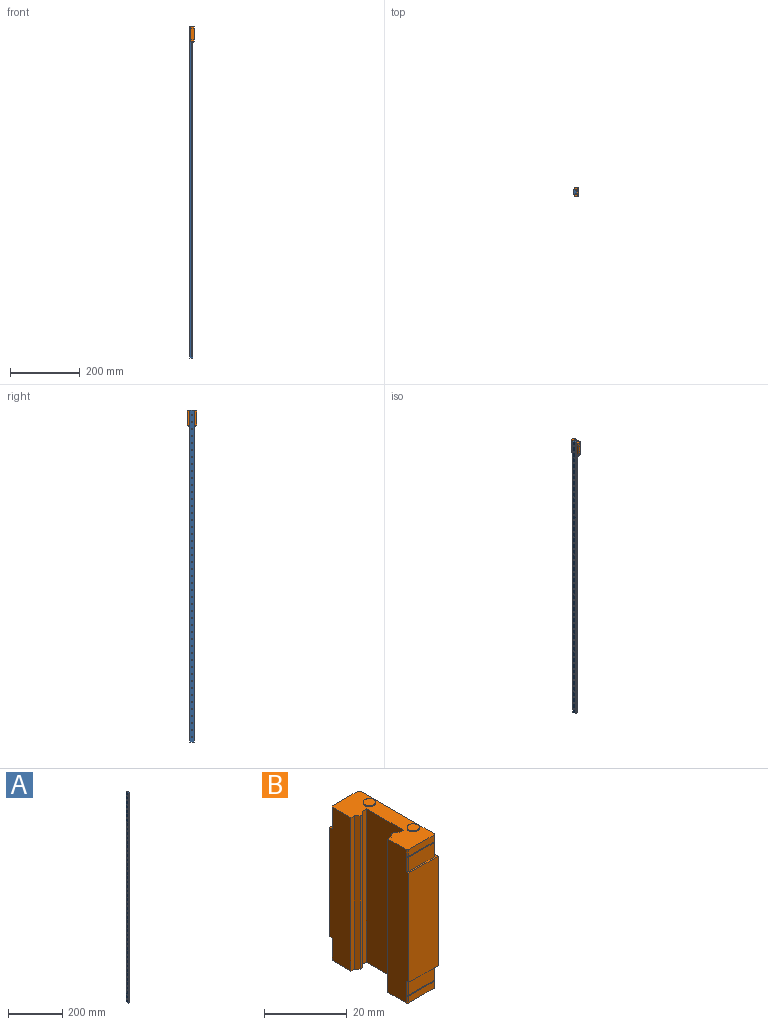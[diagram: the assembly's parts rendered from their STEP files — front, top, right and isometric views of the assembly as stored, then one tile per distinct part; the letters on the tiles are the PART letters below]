
ASSEMBLY  parts=2 mates=1
PART A: 155 faces, bbox 8x12x950 mm
  f0: plane 950x12mm, normal (1,0,0), area 10071.1mm2, adj f10,f11,f13,f15,f18,f21,f24,f27
  f1: cylinder r=1.75mm len=5.5mm, axis (-1,0,0), area 60.5mm2, adj f5,f14
  f2: plane 950x1mm, normal (0,1,0), area 950mm2, adj f3,f11,f12,f152
  f3: plane 950x1mm, normal (0.71,0.71,0), area 1343.5mm2, adj f2,f4,f11,f152
  f4: plane 950x4mm, normal (0,1,0), area 3800mm2, adj f3,f5,f11,f152
  f5: plane 950x12mm, normal (-1,0,0), area 10947.8mm2, adj f1,f4,f6,f11,f16,f19,f22,f25
  f6: plane 950x4mm, normal (0,-1,0), area 3800mm2, adj f5,f7,f11,f152
  f7: plane 950x1mm, normal (0.71,-0.71,0), area 1343.5mm2, adj f6,f8,f11,f152
  f8: plane 950x1mm, normal (0,-1,0), area 950mm2, adj f7,f9,f11,f152
  f9: plane 950x1mm, normal (-0.71,-0.71,0), area 1343.5mm2, adj f8,f10,f11,f152
  f10: plane 950x1mm, normal (0,-1,0), area 950mm2, adj f0,f9,f11,f152
  f11: plane 12x8mm, normal (0,0,-1), area 92mm2, adj f0,f2,f3,f4,f5,f6,f7,f8
  f12: plane 950x1mm, normal (-0.71,0.71,0), area 1343.5mm2, adj f2,f11,f13,f152
  f13: plane 950x1mm, normal (0,1,0), area 950mm2, adj f0,f11,f12,f152
  f14: plane 6x6mm, normal (1,0,0), area 18.7mm2, adj f1,f15
  f15: cylinder r=3mm len=6mm, axis (-1,0,0), area 47.1mm2, adj f0,f14
  f16: cylinder r=1.75mm len=5.5mm, axis (-1,0,0), area 60.5mm2, adj f5,f17
  f17: plane 6x6mm, normal (1,0,0), area 18.7mm2, adj f16,f18
  f18: cylinder r=3mm len=6mm, axis (-1,0,0), area 47.1mm2, adj f0,f17
  f19: cylinder r=1.75mm len=5.5mm, axis (-1,0,0), area 60.5mm2, adj f5,f20
  f20: plane 6x6mm, normal (1,0,0), area 18.7mm2, adj f19,f21
  f21: cylinder r=3mm len=6mm, axis (-1,0,0), area 47.1mm2, adj f0,f20
  f22: cylinder r=1.75mm len=5.5mm, axis (-1,0,0), area 60.5mm2, adj f5,f23
  f23: plane 6x6mm, normal (1,0,0), area 18.7mm2, adj f22,f24
  f24: cylinder r=3mm len=6mm, axis (-1,0,0), area 47.1mm2, adj f0,f23
  f25: cylinder r=1.75mm len=5.5mm, axis (-1,0,0), area 60.5mm2, adj f5,f26
  f26: plane 6x6mm, normal (1,0,0), area 18.7mm2, adj f25,f27
  f27: cylinder r=3mm len=6mm, axis (-1,0,0), area 47.1mm2, adj f0,f26
  f28: cylinder r=1.75mm len=5.5mm, axis (-1,0,0), area 60.5mm2, adj f5,f29
  f29: plane 6x6mm, normal (1,0,0), area 18.7mm2, adj f28,f30
  f30: cylinder r=3mm len=6mm, axis (-1,0,0), area 47.1mm2, adj f0,f29
  f31: cylinder r=1.75mm len=5.5mm, axis (-1,0,0), area 60.5mm2, adj f5,f32
  f32: plane 6x6mm, normal (1,0,0), area 18.7mm2, adj f31,f33
  f33: cylinder r=3mm len=6mm, axis (-1,0,0), area 47.1mm2, adj f0,f32
  f34: cylinder r=1.75mm len=5.5mm, axis (-1,0,0), area 60.5mm2, adj f5,f35
  f35: plane 6x6mm, normal (1,0,0), area 18.7mm2, adj f34,f36
  f36: cylinder r=3mm len=6mm, axis (-1,0,0), area 47.1mm2, adj f0,f35
  f37: cylinder r=1.75mm len=5.5mm, axis (-1,0,0), area 60.5mm2, adj f5,f38
  f38: plane 6x6mm, normal (1,0,0), area 18.7mm2, adj f37,f39
  f39: cylinder r=3mm len=6mm, axis (-1,0,0), area 47.1mm2, adj f0,f38
  f40: cylinder r=1.75mm len=5.5mm, axis (-1,0,0), area 60.5mm2, adj f5,f41
  f41: plane 6x6mm, normal (1,0,0), area 18.7mm2, adj f40,f42
  f42: cylinder r=3mm len=6mm, axis (-1,0,0), area 47.1mm2, adj f0,f41
  f43: cylinder r=1.75mm len=5.5mm, axis (-1,0,0), area 60.5mm2, adj f5,f44
  f44: plane 6x6mm, normal (1,0,0), area 18.7mm2, adj f43,f45
  f45: cylinder r=3mm len=6mm, axis (-1,0,0), area 47.1mm2, adj f0,f44
  f46: cylinder r=1.75mm len=5.5mm, axis (-1,0,0), area 60.5mm2, adj f5,f47
  f47: plane 6x6mm, normal (1,0,0), area 18.7mm2, adj f46,f48
  f48: cylinder r=3mm len=6mm, axis (-1,0,0), area 47.1mm2, adj f0,f47
  f49: cylinder r=1.75mm len=5.5mm, axis (-1,0,0), area 60.5mm2, adj f5,f50
  f50: plane 6x6mm, normal (1,0,0), area 18.7mm2, adj f49,f51
  f51: cylinder r=3mm len=6mm, axis (-1,0,0), area 47.1mm2, adj f0,f50
  f52: cylinder r=1.75mm len=5.5mm, axis (-1,0,0), area 60.5mm2, adj f5,f53
  f53: plane 6x6mm, normal (1,0,0), area 18.7mm2, adj f52,f54
  f54: cylinder r=3mm len=6mm, axis (-1,0,0), area 47.1mm2, adj f0,f53
  f55: cylinder r=1.75mm len=5.5mm, axis (-1,0,0), area 60.5mm2, adj f5,f56
  f56: plane 6x6mm, normal (1,0,0), area 18.7mm2, adj f55,f57
  f57: cylinder r=3mm len=6mm, axis (-1,0,0), area 47.1mm2, adj f0,f56
  f58: cylinder r=1.75mm len=5.5mm, axis (-1,0,0), area 60.5mm2, adj f5,f59
  f59: plane 6x6mm, normal (1,0,0), area 18.7mm2, adj f58,f60
  f60: cylinder r=3mm len=6mm, axis (-1,0,0), area 47.1mm2, adj f0,f59
  f61: cylinder r=1.75mm len=5.5mm, axis (-1,0,0), area 60.5mm2, adj f5,f62
  f62: plane 6x6mm, normal (1,0,0), area 18.7mm2, adj f61,f63
  f63: cylinder r=3mm len=6mm, axis (-1,0,0), area 47.1mm2, adj f0,f62
  f64: cylinder r=1.75mm len=5.5mm, axis (-1,0,0), area 60.5mm2, adj f5,f65
  f65: plane 6x6mm, normal (1,0,0), area 18.7mm2, adj f64,f66
  f66: cylinder r=3mm len=6mm, axis (-1,0,0), area 47.1mm2, adj f0,f65
  f67: cylinder r=1.75mm len=5.5mm, axis (-1,0,0), area 60.5mm2, adj f5,f68
  f68: plane 6x6mm, normal (1,0,0), area 18.7mm2, adj f67,f69
  f69: cylinder r=3mm len=6mm, axis (-1,0,0), area 47.1mm2, adj f0,f68
  f70: cylinder r=1.75mm len=5.5mm, axis (-1,0,0), area 60.5mm2, adj f5,f71
  f71: plane 6x6mm, normal (1,0,0), area 18.7mm2, adj f70,f72
  f72: cylinder r=3mm len=6mm, axis (-1,0,0), area 47.1mm2, adj f0,f71
  f73: cylinder r=1.75mm len=5.5mm, axis (-1,0,0), area 60.5mm2, adj f5,f74
  f74: plane 6x6mm, normal (1,0,0), area 18.7mm2, adj f73,f75
  f75: cylinder r=3mm len=6mm, axis (-1,0,0), area 47.1mm2, adj f0,f74
  f76: cylinder r=1.75mm len=5.5mm, axis (-1,0,0), area 60.5mm2, adj f5,f77
  f77: plane 6x6mm, normal (1,0,0), area 18.7mm2, adj f76,f78
  f78: cylinder r=3mm len=6mm, axis (-1,0,0), area 47.1mm2, adj f0,f77
  f79: cylinder r=1.75mm len=5.5mm, axis (-1,0,0), area 60.5mm2, adj f5,f80
  f80: plane 6x6mm, normal (1,0,0), area 18.7mm2, adj f79,f81
  f81: cylinder r=3mm len=6mm, axis (-1,0,0), area 47.1mm2, adj f0,f80
  f82: cylinder r=1.75mm len=5.5mm, axis (-1,0,0), area 60.5mm2, adj f5,f83
  f83: plane 6x6mm, normal (1,0,0), area 18.7mm2, adj f82,f84
  f84: cylinder r=3mm len=6mm, axis (-1,0,0), area 47.1mm2, adj f0,f83
  f85: cylinder r=1.75mm len=5.5mm, axis (-1,0,0), area 60.5mm2, adj f5,f86
  f86: plane 6x6mm, normal (1,0,0), area 18.7mm2, adj f85,f87
  f87: cylinder r=3mm len=6mm, axis (-1,0,0), area 47.1mm2, adj f0,f86
  f88: cylinder r=1.75mm len=5.5mm, axis (-1,0,0), area 60.5mm2, adj f5,f89
  f89: plane 6x6mm, normal (1,0,0), area 18.7mm2, adj f88,f90
  f90: cylinder r=3mm len=6mm, axis (-1,0,0), area 47.1mm2, adj f0,f89
  f91: cylinder r=1.75mm len=5.5mm, axis (-1,0,0), area 60.5mm2, adj f5,f92
  f92: plane 6x6mm, normal (1,0,0), area 18.7mm2, adj f91,f93
  f93: cylinder r=3mm len=6mm, axis (-1,0,0), area 47.1mm2, adj f0,f92
  f94: cylinder r=1.75mm len=5.5mm, axis (-1,0,0), area 60.5mm2, adj f5,f95
  f95: plane 6x6mm, normal (1,0,0), area 18.7mm2, adj f94,f96
  f96: cylinder r=3mm len=6mm, axis (-1,0,0), area 47.1mm2, adj f0,f95
  f97: cylinder r=1.75mm len=5.5mm, axis (-1,0,0), area 60.5mm2, adj f5,f98
  f98: plane 6x6mm, normal (1,0,0), area 18.7mm2, adj f97,f99
  f99: cylinder r=3mm len=6mm, axis (-1,0,0), area 47.1mm2, adj f0,f98
  f100: cylinder r=1.75mm len=5.5mm, axis (-1,0,0), area 60.5mm2, adj f5,f101
  f101: plane 6x6mm, normal (1,0,0), area 18.7mm2, adj f100,f102
  f102: cylinder r=3mm len=6mm, axis (-1,0,0), area 47.1mm2, adj f0,f101
  f103: cylinder r=1.75mm len=5.5mm, axis (-1,0,0), area 60.5mm2, adj f5,f104
  f104: plane 6x6mm, normal (1,0,0), area 18.7mm2, adj f103,f105
  f105: cylinder r=3mm len=6mm, axis (-1,0,0), area 47.1mm2, adj f0,f104
  f106: cylinder r=1.75mm len=5.5mm, axis (-1,0,0), area 60.5mm2, adj f5,f107
  f107: plane 6x6mm, normal (1,0,0), area 18.7mm2, adj f106,f108
  f108: cylinder r=3mm len=6mm, axis (-1,0,0), area 47.1mm2, adj f0,f107
  f109: cylinder r=1.75mm len=5.5mm, axis (-1,0,0), area 60.5mm2, adj f5,f110
  f110: plane 6x6mm, normal (1,0,0), area 18.7mm2, adj f109,f111
  f111: cylinder r=3mm len=6mm, axis (-1,0,0), area 47.1mm2, adj f0,f110
  f112: cylinder r=1.75mm len=5.5mm, axis (-1,0,0), area 60.5mm2, adj f5,f113
  f113: plane 6x6mm, normal (1,0,0), area 18.7mm2, adj f112,f114
  f114: cylinder r=3mm len=6mm, axis (-1,0,0), area 47.1mm2, adj f0,f113
  f115: cylinder r=1.75mm len=5.5mm, axis (-1,0,0), area 60.5mm2, adj f5,f116
  f116: plane 6x6mm, normal (1,0,0), area 18.7mm2, adj f115,f117
  f117: cylinder r=3mm len=6mm, axis (-1,0,0), area 47.1mm2, adj f0,f116
  f118: cylinder r=1.75mm len=5.5mm, axis (-1,0,0), area 60.5mm2, adj f5,f119
  f119: plane 6x6mm, normal (1,0,0), area 18.7mm2, adj f118,f120
  f120: cylinder r=3mm len=6mm, axis (-1,0,0), area 47.1mm2, adj f0,f119
  f121: cylinder r=1.75mm len=5.5mm, axis (-1,0,0), area 60.5mm2, adj f5,f122
  f122: plane 6x6mm, normal (1,0,0), area 18.7mm2, adj f121,f123
  f123: cylinder r=3mm len=6mm, axis (-1,0,0), area 47.1mm2, adj f0,f122
  f124: cylinder r=1.75mm len=5.5mm, axis (-1,0,0), area 60.5mm2, adj f5,f125
  f125: plane 6x6mm, normal (1,0,0), area 18.7mm2, adj f124,f126
  f126: cylinder r=3mm len=6mm, axis (-1,0,0), area 47.1mm2, adj f0,f125
  f127: cylinder r=1.75mm len=5.5mm, axis (-1,0,0), area 60.5mm2, adj f5,f128
  f128: plane 6x6mm, normal (1,0,0), area 18.7mm2, adj f127,f129
  f129: cylinder r=3mm len=6mm, axis (-1,0,0), area 47.1mm2, adj f0,f128
  f130: cylinder r=1.75mm len=5.5mm, axis (-1,0,0), area 60.5mm2, adj f5,f131
  f131: plane 6x6mm, normal (1,0,0), area 18.7mm2, adj f130,f132
  f132: cylinder r=3mm len=6mm, axis (-1,0,0), area 47.1mm2, adj f0,f131
  f133: cylinder r=1.75mm len=5.5mm, axis (-1,0,0), area 60.5mm2, adj f5,f134
  f134: plane 6x6mm, normal (1,0,0), area 18.7mm2, adj f133,f135
  f135: cylinder r=3mm len=6mm, axis (-1,0,0), area 47.1mm2, adj f0,f134
  f136: cylinder r=1.75mm len=5.5mm, axis (-1,0,0), area 60.5mm2, adj f5,f137
  f137: plane 6x6mm, normal (1,0,0), area 18.7mm2, adj f136,f138
  f138: cylinder r=3mm len=6mm, axis (-1,0,0), area 47.1mm2, adj f0,f137
  f139: cylinder r=1.75mm len=5.5mm, axis (-1,0,0), area 60.5mm2, adj f5,f140
  f140: plane 6x6mm, normal (1,0,0), area 18.7mm2, adj f139,f141
  f141: cylinder r=3mm len=6mm, axis (-1,0,0), area 47.1mm2, adj f0,f140
  f142: cylinder r=1.75mm len=5.5mm, axis (-1,0,0), area 60.5mm2, adj f5,f143
  f143: plane 6x6mm, normal (1,0,0), area 18.7mm2, adj f142,f144
  f144: cylinder r=3mm len=6mm, axis (-1,0,0), area 47.1mm2, adj f0,f143
  f145: cylinder r=1.75mm len=5.5mm, axis (-1,0,0), area 60.5mm2, adj f5,f146
  f146: plane 6x6mm, normal (1,0,0), area 18.7mm2, adj f145,f147
  f147: cylinder r=3mm len=6mm, axis (-1,0,0), area 47.1mm2, adj f0,f146
  f148: cylinder r=1.75mm len=5.5mm, axis (-1,0,0), area 60.5mm2, adj f5,f149
  f149: plane 6x6mm, normal (1,0,0), area 18.7mm2, adj f148,f150
  f150: cylinder r=3mm len=6mm, axis (-1,0,0), area 47.1mm2, adj f0,f149
  f151: cylinder r=1.75mm len=5.5mm, axis (-1,0,0), area 60.5mm2, adj f5,f153
  f152: plane 12x8mm, normal (0,0,1), area 92mm2, adj f0,f2,f3,f4,f5,f6,f7,f8
  f153: plane 6x6mm, normal (1,0,0), area 18.7mm2, adj f151,f154
  f154: cylinder r=3mm len=6mm, axis (-1,0,0), area 47.1mm2, adj f0,f153
PART B: 82 faces, bbox 10x27x46 mm
  f0: plane 25.29x3.9mm, normal (1,0,0), area 98.6mm2, adj f19,f48,f53,f61
  f1: plane 32.4x13mm, normal (1,0,0), area 421.2mm2, adj f21,f24,f25,f38
  f2: plane 25.29x3.9mm, normal (1,0,0), area 98.6mm2, adj f12,f13,f58,f63
  f3: plane 25.29x2mm, normal (1,0,0), area 50.6mm2, adj f11,f14,f42,f56
  f4: plane 25.29x2mm, normal (1,0,0), area 50.6mm2, adj f18,f45,f49,f55
  f5: plane 8.79x4.2mm, normal (0,1,0), area 36.9mm2, adj f10,f12,f38,f58
  f6: plane 8.79x4.2mm, normal (0,-1,0), area 36.9mm2, adj f13,f15,f38,f58
  f7: plane 8.79x2mm, normal (0,-1,0), area 17.6mm2, adj f17,f18,f45,f55
  f8: plane 8.79x2mm, normal (0,1,0), area 17.6mm2, adj f45,f49,f51,f55
  f9: plane 2x0.35mm, normal (-0.71,0.71,0), area 1mm2, adj f28,f42,f43,f56
  f10: plane 4.2x0.35mm, normal (-0.71,0.71,0), area 2.1mm2, adj f5,f28,f38,f58
  f11: plane 2x0.35mm, normal (0.71,0.71,0), area 1mm2, adj f3,f42,f43,f56
  f12: plane 4.2x0.35mm, normal (0.71,0.71,0), area 2mm2, adj f2,f5,f38,f58,f63,f64
  f13: plane 4.2x0.35mm, normal (0.71,-0.71,0), area 2mm2, adj f2,f6,f38,f58,f63,f64
  f14: plane 2x0.35mm, normal (0.71,-0.71,0), area 1mm2, adj f3,f42,f44,f56
  f15: plane 4.2x0.35mm, normal (-0.71,-0.71,0), area 2.1mm2, adj f6,f38,f40,f58
  f16: plane 2x0.35mm, normal (-0.71,-0.71,0), area 1mm2, adj f40,f42,f44,f56
  f17: plane 2x0.35mm, normal (-0.71,-0.71,0), area 1mm2, adj f7,f40,f45,f55
  f18: plane 2x0.35mm, normal (0.71,-0.71,0), area 1mm2, adj f4,f7,f45,f55
  f19: plane 4.2x0.35mm, normal (0.71,0.71,0), area 2mm2, adj f0,f21,f50,f53,f60,f61
  f20: plane 4.2x0.35mm, normal (-0.71,0.71,0), area 2.1mm2, adj f21,f28,f50,f53
  f21: plane 27x10mm, normal (0,0,1), area 24.4mm2, adj f1,f19,f20,f22,f23,f24,f25,f26
  f22: plane 32.4x10mm, normal (0,-1,0), area 324mm2, adj f21,f23,f38,f40
  f23: plane 32.4x7mm, normal (1,0,0), area 212.7mm2, adj f21,f22,f24,f38,f79,f81
  f24: plane 32.4x0.5mm, normal (0,1,0), area 16.2mm2, adj f1,f21,f23,f38
  f25: plane 32.4x0.5mm, normal (0,-1,0), area 16.2mm2, adj f1,f21,f26,f38
  f26: plane 32.4x7mm, normal (1,0,0), area 212.7mm2, adj f21,f25,f27,f38,f75,f77
  f27: plane 32.4x10mm, normal (0,1,0), area 324mm2, adj f21,f26,f28,f38
  f28: plane 45.4x7.2mm, normal (-1,0,0), area 315.8mm2, adj f9,f10,f20,f21,f27,f29,f38,f42
  f29: plane 45.4x1.12mm, normal (0,-1,0), area 51mm2, adj f28,f30,f42,f45
  f30: plane 45.4x1mm, normal (-0.71,-0.71,0), area 64.2mm2, adj f29,f31,f42,f45
  f31: plane 45.4x0.75mm, normal (0,-1,0), area 34.1mm2, adj f30,f32,f42,f45
  f32: plane 45.4x1mm, normal (0.71,-0.71,0), area 64.2mm2, adj f31,f33,f42,f45
  f33: plane 45.4x1.42mm, normal (0,-1,0), area 64.7mm2, adj f32,f34,f42,f45
  f34: plane 45.4x12.6mm, normal (-1,0,0), area 572mm2, adj f33,f35,f42,f45
  f35: plane 45.4x1.42mm, normal (0,1,0), area 64.7mm2, adj f34,f36,f42,f45
  f36: plane 45.4x1mm, normal (0.71,0.71,0), area 64.2mm2, adj f35,f37,f42,f45
  f37: plane 45.4x0.75mm, normal (0,1,0), area 34.1mm2, adj f36,f39,f42,f45
  f38: plane 27x10mm, normal (0,0,-1), area 24.4mm2, adj f1,f5,f6,f10,f12,f13,f15,f22
  f39: plane 45.4x1mm, normal (-0.71,0.71,0), area 64.2mm2, adj f37,f41,f42,f45
  f40: plane 45.4x7.2mm, normal (-1,0,0), area 315.8mm2, adj f15,f16,f17,f21,f22,f38,f41,f42
  f41: plane 45.4x1.12mm, normal (0,1,0), area 51mm2, adj f39,f40,f42,f45
  f42: plane 26x9.5mm, normal (0,0,-1), area 169.3mm2, adj f3,f9,f11,f14,f16,f28,f29,f30
  f43: plane 8.79x2mm, normal (0,1,0), area 17.6mm2, adj f9,f11,f42,f56
  f44: plane 8.79x2mm, normal (0,-1,0), area 17.6mm2, adj f14,f16,f42,f56
  f45: plane 26x9.5mm, normal (0,0,1), area 169.3mm2, adj f4,f7,f8,f17,f18,f28,f29,f30
  f46: plane 4.2x0.35mm, normal (-0.71,-0.71,0), area 2.1mm2, adj f21,f40,f47,f53
  f47: plane 8.79x4.2mm, normal (0,-1,0), area 36.9mm2, adj f21,f46,f48,f53
  f48: plane 4.2x0.35mm, normal (0.71,-0.71,0), area 2mm2, adj f0,f21,f47,f53,f60,f61
  f49: plane 2x0.35mm, normal (0.71,0.71,0), area 1mm2, adj f4,f8,f45,f55
  f50: plane 8.79x4.2mm, normal (0,1,0), area 36.9mm2, adj f19,f20,f21,f53
  f51: plane 2x0.35mm, normal (-0.71,0.71,0), area 1mm2, adj f8,f28,f45,f55
  f52: plane 9.2x0.3mm, normal (0,1,0), area 2.8mm2, adj f28,f53,f55,f65
  f53: plane 26x9.5mm, normal (0,0,1), area 14.1mm2, adj f0,f19,f20,f46,f47,f48,f50,f52
  f54: plane 9.2x0.3mm, normal (0,-1,0), area 2.8mm2, adj f40,f53,f55,f65
  f55: plane 26x9.5mm, normal (0,0,-1), area 14.1mm2, adj f4,f7,f8,f17,f18,f49,f51,f52
  f56: plane 26x9.5mm, normal (0,0,1), area 14.1mm2, adj f3,f9,f11,f14,f16,f43,f44,f57
  f57: plane 9.2x0.3mm, normal (0,-1,0), area 2.8mm2, adj f40,f56,f58,f62
  f58: plane 26x9.5mm, normal (0,0,-1), area 14.1mm2, adj f2,f5,f6,f10,f12,f13,f15,f57
  f59: plane 9.2x0.3mm, normal (0,1,0), area 2.8mm2, adj f28,f56,f58,f62
  f60: plane 25.89x0.3mm, normal (1,0,0), area 7.8mm2, adj f19,f21,f48,f61
  f61: plane 25.89x0.3mm, normal (0,0,-1), area 7.7mm2, adj f0,f19,f48,f60
  f62: plane 25.29x0.3mm, normal (1,0,0), area 7.6mm2, adj f56,f57,f58,f59
  f63: plane 25.89x0.3mm, normal (0,0,1), area 7.7mm2, adj f2,f12,f13,f64
  f64: plane 25.89x0.3mm, normal (1,0,0), area 7.8mm2, adj f12,f13,f38,f63
  f65: plane 25.29x0.3mm, normal (1,0,0), area 7.6mm2, adj f52,f53,f54,f55
  f66: plane 3x3mm, normal (0,0,1), area 7.1mm2, adj f67
  f67: cylinder r=1.5mm len=3mm, axis (0,0,-1), area 2.8mm2, adj f45,f66
  f68: cylinder r=1.5mm len=3mm, axis (0,0,-1), area 2.8mm2, adj f42,f69
  f69: plane 3x3mm, normal (0,0,-1), area 7.1mm2, adj f68
  f70: plane 3x3mm, normal (0,0,1), area 7.1mm2, adj f71
  f71: cylinder r=1.5mm len=3mm, axis (0,0,-1), area 2.8mm2, adj f45,f70
  f72: cylinder r=1.5mm len=3mm, axis (0,0,-1), area 2.8mm2, adj f42,f73
  f73: plane 3x3mm, normal (0,0,-1), area 7.1mm2, adj f72
  f74: plane 3x3mm, normal (1,0,0), area 7.1mm2, adj f75
  f75: cylinder r=1.5mm len=3.5mm, axis (-1,0,0), area 33mm2, adj f26,f74
  f76: plane 3x3mm, normal (1,0,0), area 7.1mm2, adj f77
  f77: cylinder r=1.5mm len=3.5mm, axis (-1,0,0), area 33mm2, adj f26,f76
  f78: plane 3x3mm, normal (1,0,0), area 7.1mm2, adj f79
  f79: cylinder r=1.5mm len=3.5mm, axis (-1,0,0), area 33mm2, adj f23,f78
  f80: plane 3x3mm, normal (1,0,0), area 7.1mm2, adj f81
  f81: cylinder r=1.5mm len=3.5mm, axis (-1,0,0), area 33mm2, adj f23,f80
PLACE A at identity fixed
PLACE B t=(0,122,922.3)mm
MATE slider B.f42 <-> A.f11  axis (0,0,-1) through (8.3,100,899.6)mm
